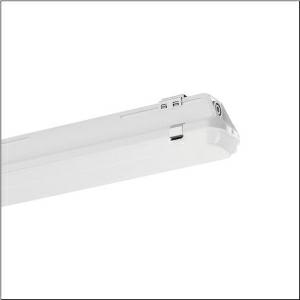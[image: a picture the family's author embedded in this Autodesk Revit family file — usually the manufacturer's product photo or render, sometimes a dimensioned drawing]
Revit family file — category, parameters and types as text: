
# Revit family: monsun_11_51fp10mp680l
name_source: partatom
category: Lighting Fixtures
units: mm (PartAtom-declared; Revit-internal decimal feet)

## family parameters
Cut with Voids When Loaded = No
Host = Face
Light Source = No
Part Type = Normal
Room Calculation Point = No
Round Connector Dimension = Use Diameter
Shared = No

## types (1)
- --- (1 x LED, 7970 lm, 45.1 W, 6500K)
    Apparent Load = 45 VA
    CIE Flux Codes = 47 77 93 94 100
    Color Rendering = 80
    Color Temperature = 6500K
    Default Elevation = 1800 mm
    Description = Monsun 11, damp-proof luminaire, chain hanger, primary optical cover: enclosure, of PMMA, light emission: direct distribution, primary light characteristic: symmetric, installation type: suspended mounting, surface-mounted, horizontal mounting, vertical mounting, LED, rated luminous flux: 7.970lm, luminous efficacy: 177lm/W, light colour: 865, colour temperature: 6500K, control gear: ON/OFF Multilumen, with terminal, 3-pole, max. 2.5mm², mains connection: 220..240V, AC, 50/60Hz, rated input power: 45W, luminaire housing, of glass-fibre reinforced polyester, uncoated, bright grey, incl. chain hanger, length: 1.590mm, width: 90mm, height: 88mm, clip for enclosure, of stainless steel (V2A), ceiling mounting element, of stainless steel (V2A), chain hanger, of stainless steel (V2A), protection rating (complete): IP66, insulation class (complete): insulation class I (protective earthing), certification: CE, ENEC, VDE, UKCA, protection symbol: D, impact resistance: IK04, permissible operating ambient temperature: -35..+40°C, standard: EN 50419, EN 60598-2-1, contact your sales advisor before using the luminaires in applications with unclear chemical exposure, large temperature fluctuations or condensation-forming humidity, LABS conformity tested according to VDMA 24364:2018-05, no direct snow, no direct sun, no direct rain, for indoor or canopied outdoor use, corresponds to IFS (International Featured Standards) requirements for safety and quality in the food industry, packaging unit: 1 piece
    Height = 89 mm
    Lamp = 1 x LED
    Lamp Light Flux = 7970 lm
    Lamp Power = 45.1 W
    Lamp count = 1
    Length = 1590 mm
    Luminous efficacy = 177 lm/W
    Manufacturer = Siteco
    ModVariant = No
    Model = 51FP10MP680L
    Mounting Place = Ceiling
    Mounting Type = Surface mounted
    Number of Poles = 1
    OnlyDefault = Yes
    Power Factor = 1
    Product Name = Monsun 11
    Product group = damp-proof luminaire
    ProductGroupID = 300
    Protection Class = Protection class I
    Protection Degree = IP 66
    RLX_Detail_Level = 1
    RLX_Emergency_Light_Flux = 0 lm
    RLX_Emergency_Type = 0
    RLX_Emergency_Type_DB = No
    RlxData = <blob elided: 89993 chars, md5=7ae63f64>
    Socket = socket
    Standby Power = 0 W
    System Light Flux = 7970 lm
    System Power = 45 W
    Type Comments = factory setting: luminous flux: 100 % | (A | C | E) | 103 mA
    Type Image = l_1349237.jpg
    URL = http://relux.com
    VarID = @adj_030459
    Voltage = 0 V
    Weight = 0.00 kg
    Width = 90 mm

## geometry (parser evidence)
native form markers: Blend x4, Sweep x15
no freeform markers — native parametric forms only
